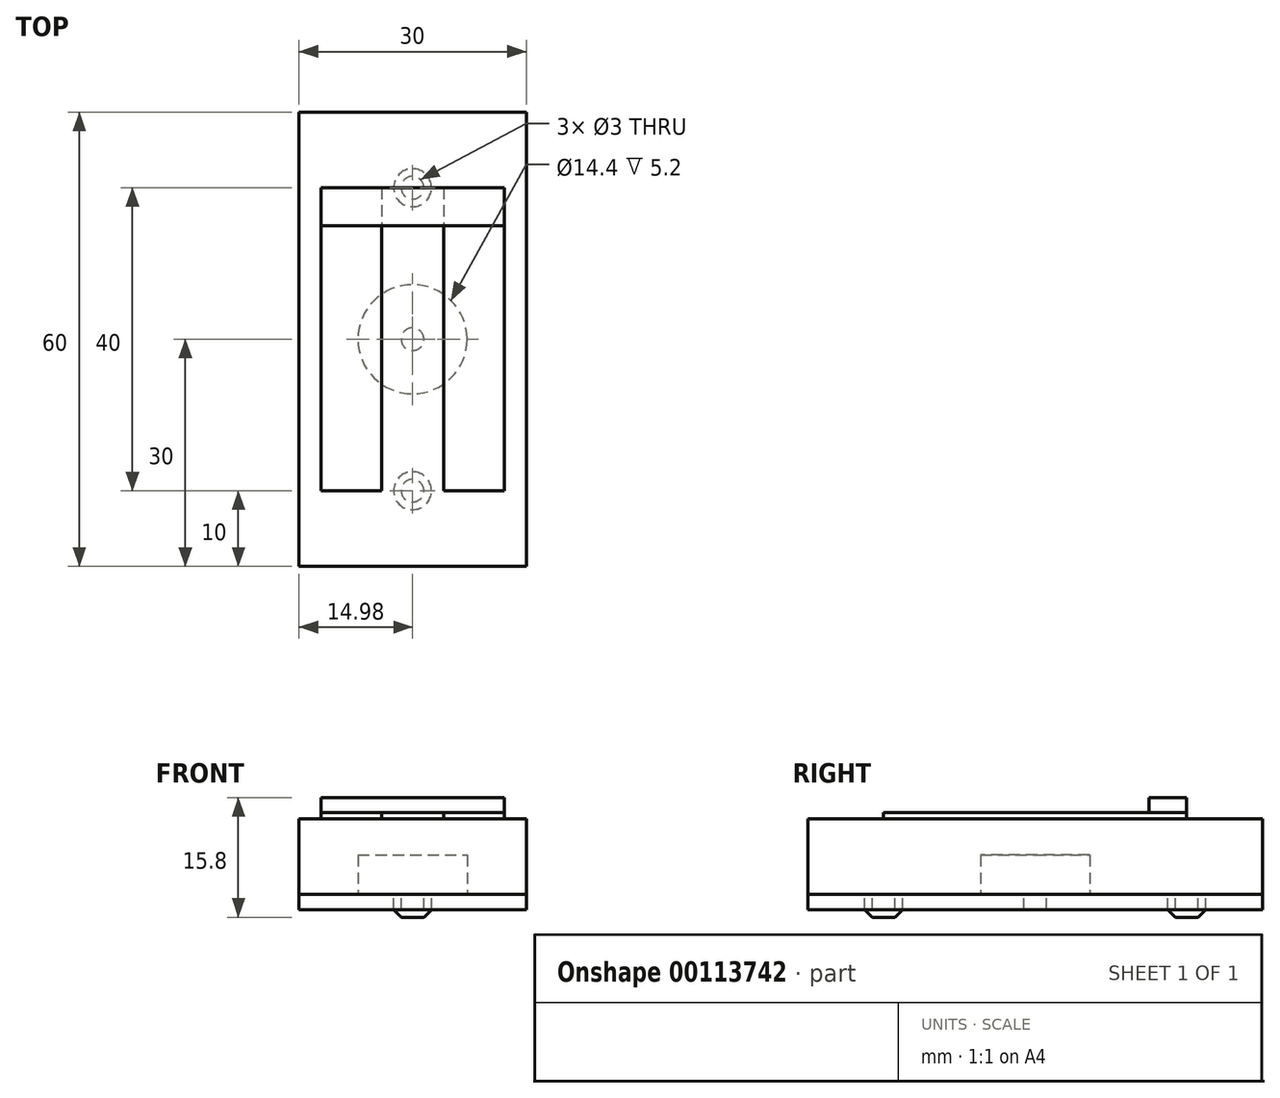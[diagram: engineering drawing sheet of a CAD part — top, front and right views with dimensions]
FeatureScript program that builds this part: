
annotation { "Feature Type Name" : "Feature", "Feature Type Description" : "" }
export const myFeature = defineFeature(function(context is Context, id is Id, definition is map)
    precondition{}
    {
        {
            var Q0;
            Q0=qCreatedBy(makeId("Top.planeOp"),FACE);
            var sketch = newSketch(context, id + "F0", { "sketchPlane" : qUnion([Q0])});
            skLineSegment(sketch, "E0.bottom", {"start": v(-12.1, 20) * mm, "end": v(-4.1, 20) * mm});
            skLineSegment(sketch, "E0.top", {"start": v(-12.1, -20) * mm, "end": v(-4.1, -20) * mm});
            skLineSegment(sketch, "E0.left", {"start": v(-12.1, 20) * mm, "end": v(-12.1, -20) * mm});
            skLineSegment(sketch, "E0.right", {"start": v(-4.1, 20) * mm, "end": v(-4.1, -20) * mm});
            skLineSegment(sketch, "E1.MirrorCS", {"start": v(4.1, 20) * mm, "end": v(4.1, -20) * mm});
            skLineSegment(sketch, "E2.MirrorCS", {"start": v(12.1, 20) * mm, "end": v(12.1, -20) * mm});
            skLineSegment(sketch, "E3.MirrorCS", {"start": v(12.1, -20) * mm, "end": v(4.1, -20) * mm});
            skLineSegment(sketch, "E4.MirrorCS", {"start": v(12.1, 20) * mm, "end": v(4.1, 20) * mm});
            skSolve(sketch);
        }
        {
            var Q0;
            Q0 = qSketchRegion(id + "F0", true);
            extrude(context, id + "F1", {"entities" : qUnion([Q0]), "depth" : 0.8 * mm});
        }
        {
            var Q0;
            Q0=makeQuery(id+"F1.opExtrude","CAP_FACE",FACE,{"disambiguationData":[OSD([sQuery(id+"F0.wireOp",EDGE,"E0.bottom"),sQuery(id+"F0.wireOp",EDGE,"E0.top"),sQuery(id+"F0.wireOp",EDGE,"E0.left"),sQuery(id+"F0.wireOp",EDGE,"E0.right")])],"isStart":true});
            var sketch = newSketch(context, id + "F2", { "sketchPlane" : qUnion([Q0])});
            skLineSegment(sketch, "E5.bottom", {"start": v(-14.98, 30) * mm, "end": v(15.02, 30) * mm});
            skLineSegment(sketch, "E5.top", {"start": v(-14.98, -30) * mm, "end": v(15.02, -30) * mm});
            skLineSegment(sketch, "E5.left", {"start": v(-14.98, 30) * mm, "end": v(-14.98, -30) * mm});
            skLineSegment(sketch, "E5.right", {"start": v(15.02, 30) * mm, "end": v(15.02, -30) * mm});
            skSolve(sketch);
        }
        {
            var Q0;
            Q0 = qSketchRegion(id + "F2", true);
            extrude(context, id + "F3", {"entities" : qUnion([Q0]), "operationType" : NewBodyOperationType.ADD, "depth" : 10 * mm});
        }
        {
            var Q0;
            Q0=makeQuery(id+"F1.opExtrude","CAP_FACE",FACE,{"disambiguationData":[OSD([sQuery(id+"F0.wireOp",EDGE,"E1.MirrorCS"),sQuery(id+"F0.wireOp",EDGE,"E2.MirrorCS"),sQuery(id+"F0.wireOp",EDGE,"E3.MirrorCS"),sQuery(id+"F0.wireOp",EDGE,"E4.MirrorCS")])],"isStart":false});
            var sketch = newSketch(context, id + "F4", { "sketchPlane" : qUnion([Q0])});
            skLineSegment(sketch, "E6.bottom", {"start": v(12.1, 20) * mm, "end": v(-12.1, 20) * mm});
            skLineSegment(sketch, "E6.top", {"start": v(12.1, 15) * mm, "end": v(-12.1, 15) * mm});
            skLineSegment(sketch, "E6.left", {"start": v(12.1, 20) * mm, "end": v(12.1, 15) * mm});
            skLineSegment(sketch, "E6.right", {"start": v(-12.1, 20) * mm, "end": v(-12.1, 15) * mm});
            skSolve(sketch);
        }
        {
            var Q0;
            Q0 = qSketchRegion(id + "F4", true);
            extrude(context, id + "F5", {"entities" : qUnion([Q0]), "depth" : 2 * mm});
        }
        {
            var Q0;
            Q0=makeQuery(id+"F3.opExtrude","CAP_FACE",FACE,{"disambiguationData":[OSD([sQuery(id+"F2.wireOp",EDGE,"E5.bottom"),sQuery(id+"F2.wireOp",EDGE,"E5.top"),sQuery(id+"F2.wireOp",EDGE,"E5.left"),sQuery(id+"F2.wireOp",EDGE,"E5.right")])],"isStart":false});
            var sketch = newSketch(context, id + "F6", { "sketchPlane" : qUnion([Q0])});
            skCircle(sketch, "E7", {"center": v(0, 0) * mm, "radius": 7.2 * mm});
            skSolve(sketch);
        }
        {
            var Q0;
            Q0 = qSketchRegion(id + "F6", true);
            extrude(context, id + "F7", {"entities" : qUnion([Q0]), "operationType" : NewBodyOperationType.REMOVE, "oppositeDirection" : true, "depth" : 5.2 * mm});
        }
        {
            var Q0;
            Q0=makeQuery(id+"F3.opExtrude","CAP_FACE",FACE,{"disambiguationData":[OSD([sQuery(id+"F2.wireOp",EDGE,"E5.bottom"),sQuery(id+"F2.wireOp",EDGE,"E5.top"),sQuery(id+"F2.wireOp",EDGE,"E5.left"),sQuery(id+"F2.wireOp",EDGE,"E5.right")])],"isStart":false});
            var sketch = newSketch(context, id + "F8", { "sketchPlane" : qUnion([Q0])});
            skCircle(sketch, "E8", {"center": v(0, 20) * mm, "radius": 2.5 * mm});
            skCircle(sketch, "E9", {"center": v(0, -20) * mm, "radius": 2.5 * mm});
            skSolve(sketch);
        }
        {
            var Q0;
            Q0 = qSketchRegion(id + "F8", true);
            extrude(context, id + "F9", {"entities" : qUnion([Q0]), "operationType" : NewBodyOperationType.ADD, "depth" : 3 * mm});
        }
        {
            var Q0;
            Q0=makeQuery(id+"F9.opExtrude","CAP_EDGE",EDGE,{"disambiguationData":[OSD([sQuery(id+"F8.wireOp",EDGE,"E8")])],"isStart":false});
            var Q1;
            Q1=makeQuery(id+"F9.opExtrude","CAP_EDGE",EDGE,{"disambiguationData":[OSD([sQuery(id+"F8.wireOp",EDGE,"E9")])],"isStart":false});
            chamfer(context, id + "F10", {"entities" : qUnion([Q0, Q1]), "width" : 1 * mm, "tangentPropagation" : true});
        }
        {
            var Q0;
            Q0=makeQuery(id+"F3.opExtrude","CAP_FACE",FACE,{"disambiguationData":[OSD([sQuery(id+"F2.wireOp",EDGE,"E5.bottom"),sQuery(id+"F2.wireOp",EDGE,"E5.top"),sQuery(id+"F2.wireOp",EDGE,"E5.left"),sQuery(id+"F2.wireOp",EDGE,"E5.right")])],"isStart":false});
            var sketch = newSketch(context, id + "F11", { "sketchPlane" : qUnion([Q0])});
            skCircle(sketch, "E10", {"center": v(0, 20) * mm, "radius": 1.5 * mm});
            skCircle(sketch, "E11", {"center": v(0, 0) * mm, "radius": 1.5 * mm});
            skCircle(sketch, "E12", {"center": v(0, -20) * mm, "radius": 1.5 * mm});
            skLineSegment(sketch, "E13.bottom", {"start": v(15.02, 30) * mm, "end": v(-14.98, 30) * mm});
            skLineSegment(sketch, "E13.top", {"start": v(15.02, -30) * mm, "end": v(-14.98, -30) * mm});
            skLineSegment(sketch, "E13.left", {"start": v(15.02, 30) * mm, "end": v(15.02, -30) * mm});
            skLineSegment(sketch, "E13.right", {"start": v(-14.98, 30) * mm, "end": v(-14.98, -30) * mm});
            skSolve(sketch);
        }
        {
            var Q0;
            Q0 = qSketchRegion(id + "F11", true);
            extrude(context, id + "F12", {"entities" : qUnion([Q0]), "depth" : 2 * mm});
        }
    });
